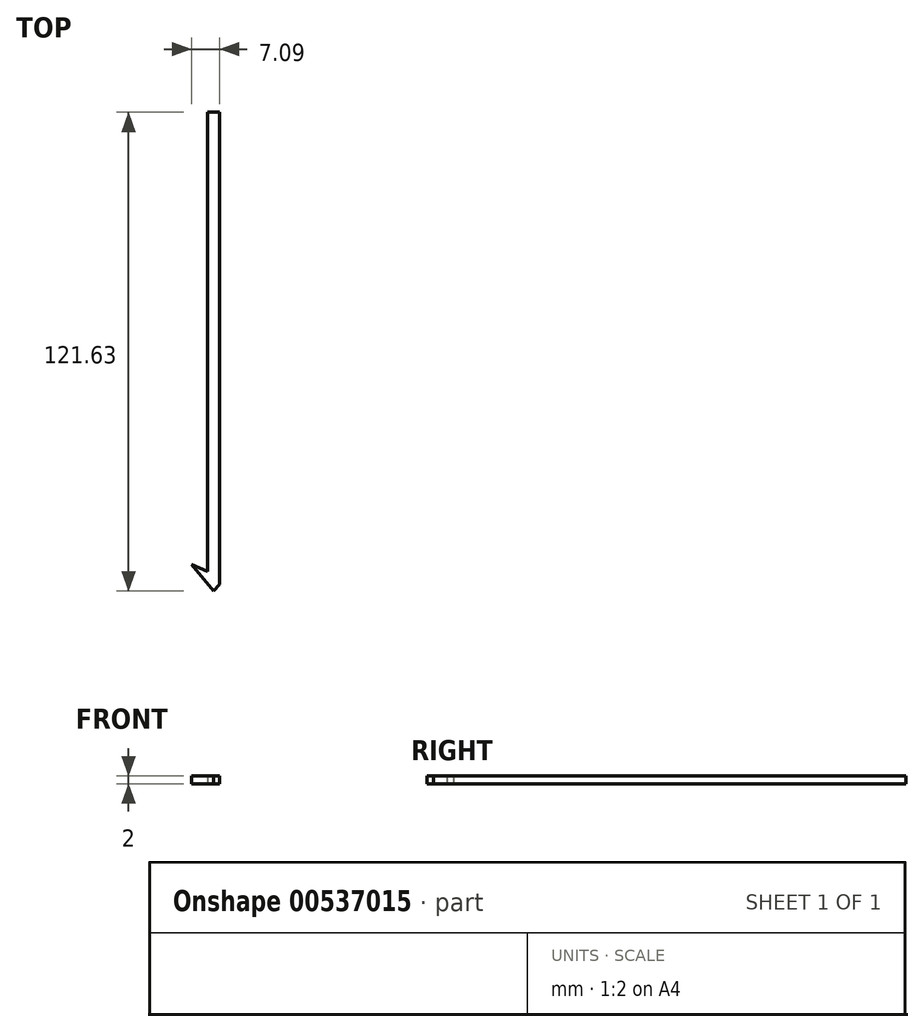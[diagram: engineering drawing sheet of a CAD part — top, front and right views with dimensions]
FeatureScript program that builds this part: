
annotation { "Feature Type Name" : "Feature", "Feature Type Description" : "" }
export const myFeature = defineFeature(function(context is Context, id is Id, definition is map)
    precondition{}
    {
        {
            var Q0;
            Q0=qCreatedBy(makeId("Top.planeOp"),FACE);
            var sketch = newSketch(context, id + "F0", { "sketchPlane" : qUnion([Q0])});
            skLineSegment(sketch, "E0.bottom", {"start": v(1.5, 60) * mm, "end": v(-1.5, 60) * mm});
            skLineSegment(sketch, "E0.left", {"start": v(1.5, 60) * mm, "end": v(1.5, -60) * mm});
            skLineSegment(sketch, "E0.right", {"start": v(-1.5, 60) * mm, "end": v(-1.5, -56.63) * mm});
            skPoint(sketch, "E0.middle", {"position": v(0, 0) * mm});
            skLineSegment(sketch, "E1", {"start": v(-5.6, -54.9) * mm, "end": v(-1.5, -56.63) * mm});
            skLineSegment(sketch, "E2", {"start": v(0, -61.63) * mm, "end": v(1.5, -60) * mm});
            skLineSegment(sketch, "E3", {"start": v(-5.6, -54.9) * mm, "end": v(0, -61.63) * mm});
            skSolve(sketch);
        }
        {
            var Q0;
            Q0=makeQuery(id+"F0.imprint","IMPRINT",FACE,{"disambiguationData":[TD([[makeQuery(id+"F0.imprint","IMPRINT",EDGE,{"derivedFrom":sQuery(id+"F0.wireOp",EDGE,"E0.bottom")}),1.0]])]});
            extrude(context, id + "F1", {"entities" : qUnion([Q0]), "depth" : 2 * mm, "offsetDistance" : 25 * mm});
        }
    });
